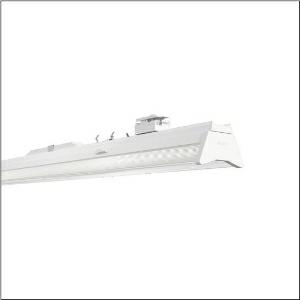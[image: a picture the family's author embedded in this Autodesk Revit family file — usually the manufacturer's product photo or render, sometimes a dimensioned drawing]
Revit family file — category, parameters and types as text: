
# Revit family: licross_r__21_performance_mo_52tm167n445g_e37c
name_source: partatom
category: Lighting Fixtures
units: mm (PartAtom-declared; Revit-internal decimal feet)

## family parameters
Cut with Voids When Loaded = No
Host = Face
Light Source = No
Part Type = Normal
Room Calculation Point = No
Round Connector Dimension = Use Diameter
Shared = No

## types (1)
- Licross® 21 Performance MO (1 x LED, 4580 lm, 24.7 W, 4000K)
    Apparent Load = 25 VA
    CIE Flux Codes = 66 88 96 79 100
    Color Rendering = 80
    Color Temperature = 4000K
    Default Elevation = 1800 mm
    Description = Licross® 21 Performance MO, luminaire insert, of sheet steel, galvanised, coil coated, white, length: 1.500mm, width: 120mm, height: 123mm, LED rated luminous flux: 4.580lm, light colour: 840, control gear: ON/OFF, control gear: ECG, with plug, 3-pole, with phase selection, mains connection: 220..240V, AC, 50/60Hz, halogen-free wiring, primary light control with lens, of plastic, primary optical cover: cover, of PMMA, CAT 2 (L<= 3000cd/m²), light emission: direct/indirect distribution, primary light characteristic: symmetric, protection rating (complete): IP40, insulation class (complete): insulation class I (protective earthing), certification: CE, ENEC, UKCA, protection symbol: D if used in an environment without relevant dust loads with corresponding accessories, impact resistance: IK06, permissible ambient temperature for indoor applications: -35..+55°C, corresponds to IFS (International Featured Standards) requirements for safety and quality in the food industry, reducing of maximum allowable ambient temperature of 5°C with ceiling mounting, LABS conformity tested according to VDMA 24364:2018-05, packaging unit: 1 piece
    Height = 114 mm
    Lamp = 1 x LED
    Lamp Light Flux = 4580 lm
    Lamp Power = 24.7 W
    Lamp count = 1
    Length = 1500 mm
    Luminous efficacy = 185 lm/W
    Manufacturer = Siteco
    ModVariant = No
    Model = 52TM167N445G
    Mounting Place = Ceiling
    Mounting Type = Pendant
    Number of Poles = 1
    OnlyDefault = Yes
    Power Factor = 1
    Product Name = Licross® 21 Performance MO
    Product group = luminaire insert
    ProductGroupID = 902
    Protection Class = Protection class I
    Protection Degree = IP 40
    RLX_Detail_Level = 1
    RlxData = <blob elided: 30349 chars, md5=025a31fa>
    Socket = socket
    Standby Power = 0 W
    System Light Flux = 4580 lm
    System Power = 25 W
    Type Comments = Product without accessories
    Type Image = l_1256138.jpg
    URL = http://relux.com
    VarID = ---
    Voltage = 0 V
    Weight = 0.00 kg
    Width = 120 mm

## geometry (parser evidence)
native form markers: Blend x4, Sweep x12
no freeform markers — native parametric forms only
